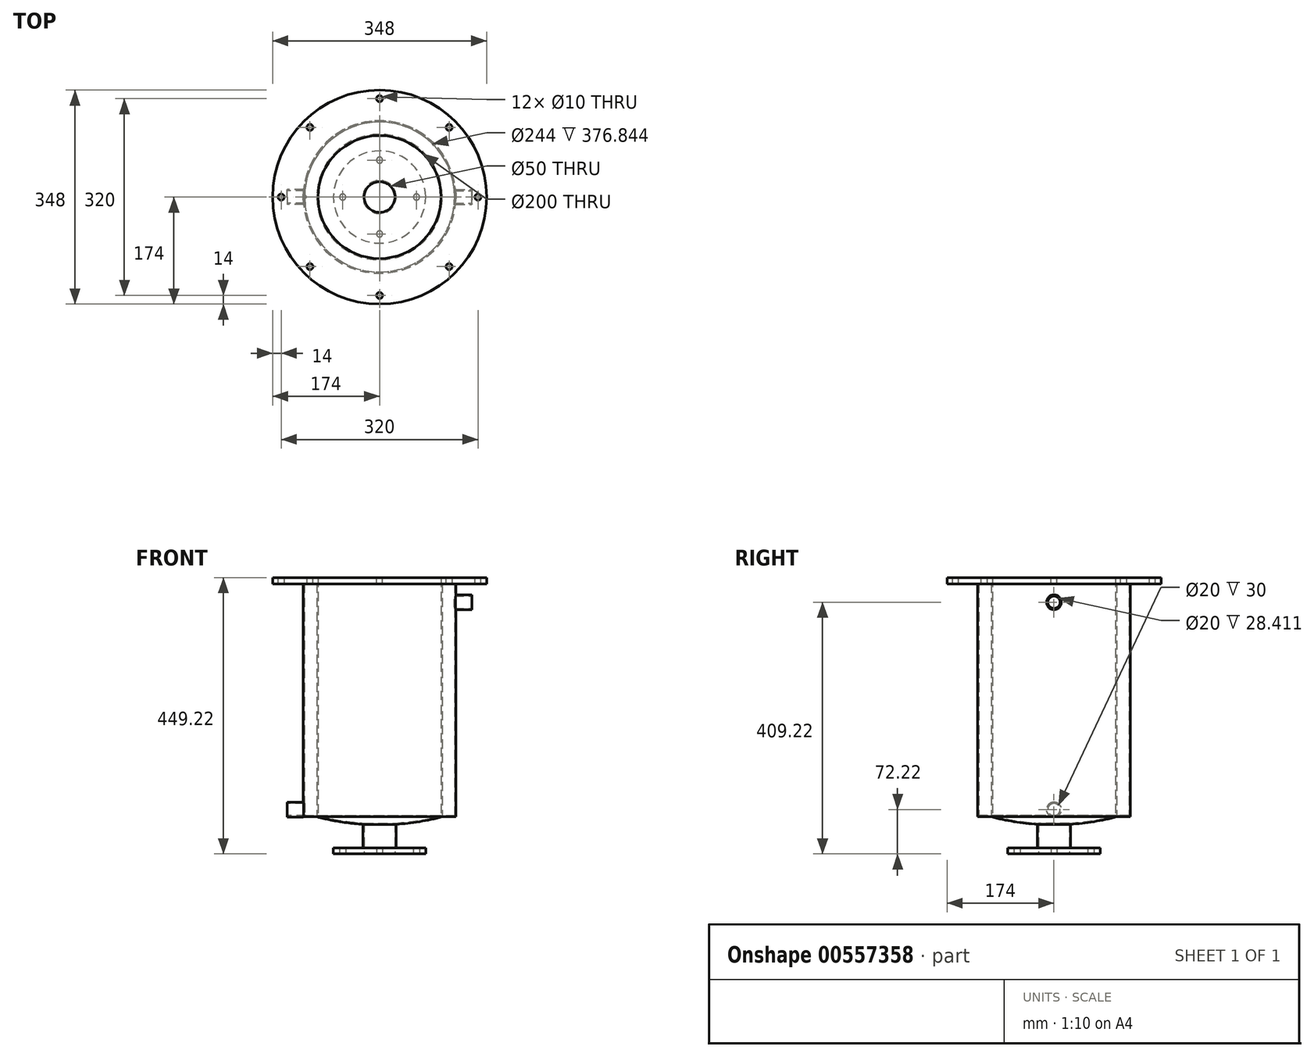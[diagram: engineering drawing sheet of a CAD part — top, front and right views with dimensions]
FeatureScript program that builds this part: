
annotation { "Feature Type Name" : "Feature", "Feature Type Description" : "" }
export const myFeature = defineFeature(function(context is Context, id is Id, definition is map)
    precondition{}
    {
        {
            var Q0;
            Q0=qCreatedBy(makeId("Front.planeOp"),FACE);
            var sketch = newSketch(context, id + "F0", { "sketchPlane" : qUnion([Q0])});
            skLineSegment(sketch, "E0", {"start": v(0, 0) * mm, "end": v(0, 400) * mm, "construction": true});
            skLineSegment(sketch, "E1", {"start": v(-100, 400) * mm, "end": v(-100, 12.7) * mm});
            skArc(sketch, "E2", {"start": v(-25, 0.78) * mm, "mid": v(-62.78, 4.96) * mm, "end": v(-100, 12.7) * mm});
            skLineSegment(sketch, "E3", {"start": v(-25, -49.22) * mm, "end": v(-25, 0.78) * mm});
            skPoint(sketch, "E4.orphan", {"position": v(-25, 22.92) * mm});
            skLineSegment(sketch, "E5.0", {"start": v(-27, -39.22) * mm, "end": v(-27, -1.1) * mm});
            skArc(sketch, "E5.1", {"start": v(-27, -1.1) * mm, "mid": v(-64.8, 3.26) * mm, "end": v(-102, 11.16) * mm});
            skLineSegment(sketch, "E5.2", {"start": v(-102, 390) * mm, "end": v(-102, 13.16) * mm});
            skLineSegment(sketch, "E6", {"start": v(-102, 400) * mm, "end": v(-100, 400) * mm});
            skLineSegment(sketch, "E7", {"start": v(-102, 11.16) * mm, "end": v(-124, 11.16) * mm});
            skLineSegment(sketch, "E8", {"start": v(-124, 11.16) * mm, "end": v(-124, 390) * mm});
            skLineSegment(sketch, "E9", {"start": v(-124, 400) * mm, "end": v(-102, 400) * mm});
            skLineSegment(sketch, "E10.1", {"start": v(-122, 13.16) * mm, "end": v(-122, 390) * mm});
            skLineSegment(sketch, "E10.2", {"start": v(-102, 13.16) * mm, "end": v(-122, 13.16) * mm});
            skLineSegment(sketch, "E11", {"start": v(-124, 400) * mm, "end": v(-174, 400) * mm});
            skLineSegment(sketch, "E12", {"start": v(-174, 400) * mm, "end": v(-174, 390) * mm});
            skLineSegment(sketch, "E13", {"start": v(-174, 390) * mm, "end": v(-124, 390) * mm});
            skLineSegment(sketch, "E14", {"start": v(-122, 390) * mm, "end": v(-102, 390) * mm});
            skLineSegment(sketch, "E15", {"start": v(-25, -49.22) * mm, "end": v(-75, -49.22) * mm});
            skLineSegment(sketch, "E16", {"start": v(-75, -49.22) * mm, "end": v(-75, -39.22) * mm});
            skLineSegment(sketch, "E17", {"start": v(-75, -39.22) * mm, "end": v(-27, -39.22) * mm});
            skSolve(sketch);
        }
        {
            var Q0;
            Q0=makeQuery(id+"F0.imprint","IMPRINT",FACE,{"disambiguationData":[TD([[makeQuery(id+"F0.imprint","IMPRINT",EDGE,{"derivedFrom":sQuery(id+"F0.wireOp",EDGE,"E1")}),-1.0]])]});
            var Q1;
            Q1=sQuery(id+"F0.wireOp",EDGE,"E0");
            revolve(context, id + "F1", {"surfaceOperationType" : NewSurfaceOperationType.NEW, "entities" : qUnion([Q0]), "axis" : qUnion([Q1]), "revolveType" : RevolveType.FULL});
        }
        {
            var Q0;
            Q0=qCreatedBy(makeId("Front.planeOp"),FACE);
            var sketch = newSketch(context, id + "F2", { "sketchPlane" : qUnion([Q0])});
            skLineSegment(sketch, "E18", {"start": v(0, 23) * mm, "end": v(-150, 23) * mm});
            skSolve(sketch);
        }
        {
            var Q0;
            Q0=qCreatedBy(makeId("Right.planeOp"),FACE);
            cPlane(context, id + "F3", {"entities" : qUnion([Q0]), "cplaneType" : CPlaneType.OFFSET, "offset" : 150 * mm, "oppositeDirection" : true, "width" : 150 * mm, "height" : 150 * mm});
        }
        {
            var Q0;
            Q0=qCreatedBy(id+"F3.planeOp",FACE);
            var sketch = newSketch(context, id + "F4", { "sketchPlane" : qUnion([Q0])});
            skCircle(sketch, "E19", {"center": v(0, 23) * mm, "radius": 10 * mm});
            skSolve(sketch);
        }
        {
            var Q0;
            Q0=qCreatedBy(id+"F3.planeOp",FACE);
            var sketch = newSketch(context, id + "F5", { "sketchPlane" : qUnion([Q0])});
            skCircle(sketch, "E20", {"center": v(0, 23) * mm, "radius": 12 * mm});
            skSolve(sketch);
        }
        {
            var Q0;
            Q0=makeQuery(id+"F5.imprint","IMPRINT",FACE,{"disambiguationData":[TD([[makeQuery(id+"F5.imprint","IMPRINT",EDGE,{"derivedFrom":sQuery(id+"F5.wireOp",EDGE,"E20")}),1.0]])]});
            var Q1;
            Q1=makeQuery(id+"F1.opRevolve","SWEPT_FACE",FACE,{"disambiguationData":[OSD([sQuery(id+"F0.wireOp",EDGE,"E8")])]});
            extrude(context, id + "F6", {"entities" : qUnion([Q0]), "operationType" : NewBodyOperationType.ADD, "endBound" : BoundingType.UP_TO_SURFACE, "depth" : 25 * mm, "endBoundEntityFace" : qUnion([Q1]), "offsetDistance" : 25 * mm});
        }
        {
            var Q0;
            Q0=makeQuery(id+"F4.imprint","IMPRINT",FACE,{"disambiguationData":[TD([[makeQuery(id+"F4.imprint","IMPRINT",EDGE,{"derivedFrom":sQuery(id+"F4.wireOp",EDGE,"E19")}),1.0]])]});
            extrude(context, id + "F7", {"entities" : qUnion([Q0]), "operationType" : NewBodyOperationType.REMOVE, "depth" : 30 * mm, "offsetDistance" : 25 * mm});
        }
        {
            var Q0;
            Q0=qCreatedBy(makeId("Right.planeOp"),FACE);
            cPlane(context, id + "F8", {"entities" : qUnion([Q0]), "cplaneType" : CPlaneType.OFFSET, "offset" : 150 * mm, "width" : 150 * mm, "height" : 150 * mm});
        }
        {
            var Q0;
            Q0=qCreatedBy(id+"F8.planeOp",FACE);
            var sketch = newSketch(context, id + "F9", { "sketchPlane" : qUnion([Q0])});
            skCircle(sketch, "E21", {"center": v(0, 360) * mm, "radius": 12 * mm});
            skCircle(sketch, "E22", {"center": v(0, 360) * mm, "radius": 10 * mm});
            skSolve(sketch);
        }
        {
            var Q0;
            Q0=makeQuery(id+"F9.imprint","IMPRINT",FACE,{"disambiguationData":[TD([[makeQuery(id+"F9.imprint","IMPRINT",EDGE,{"derivedFrom":sQuery(id+"F9.wireOp",EDGE,"E21")}),1.0]])]});
            var Q1;
            Q1=makeQuery(id+"F1.opRevolve","SWEPT_FACE",FACE,{"disambiguationData":[OSD([sQuery(id+"F0.wireOp",EDGE,"E8")])]});
            extrude(context, id + "F10", {"entities" : qUnion([Q0]), "operationType" : NewBodyOperationType.ADD, "endBound" : BoundingType.UP_TO_SURFACE, "oppositeDirection" : true, "depth" : 25 * mm, "endBoundEntityFace" : qUnion([Q1]), "offsetDistance" : 25 * mm});
        }
        {
            var Q0;
            Q0=qCreatedBy(id+"F8.planeOp",FACE);
            var sketch = newSketch(context, id + "F11", { "sketchPlane" : qUnion([Q0])});
            skCircle(sketch, "E23", {"center": v(0, 360) * mm, "radius": 10 * mm});
            skSolve(sketch);
        }
        {
            var Q0;
            Q0=makeQuery(id+"F11.imprint","IMPRINT",FACE,{"disambiguationData":[TD([[makeQuery(id+"F11.imprint","IMPRINT",EDGE,{"derivedFrom":sQuery(id+"F11.wireOp",EDGE,"E23")}),1.0]])]});
            extrude(context, id + "F12", {"entities" : qUnion([Q0]), "operationType" : NewBodyOperationType.REMOVE, "oppositeDirection" : true, "depth" : 30 * mm, "offsetDistance" : 25 * mm});
        }
        {
            var Q0;
            Q0=makeQuery(id+"F1.opRevolve","SWEPT_FACE",FACE,{"disambiguationData":[OSD([sQuery(id+"F0.wireOp",EDGE,"E15")])]});
            var sketch = newSketch(context, id + "F13", { "sketchPlane" : qUnion([Q0])});
            skCircle(sketch, "E24", {"center": v(0, 60) * mm, "radius": 5 * mm});
            skCircle(sketch, "E25.1.0", {"center": v(-60, 0) * mm, "radius": 5 * mm});
            skCircle(sketch, "E25.2.0", {"center": v(0, -60) * mm, "radius": 5 * mm});
            skCircle(sketch, "E25.3.0", {"center": v(60, 0) * mm, "radius": 5 * mm});
            skPoint(sketch, "E25.center", {"position": v(0, 0) * mm});
            skSolve(sketch);
        }
        {
            var Q0;
            Q0=makeQuery(id+"F13.imprint","IMPRINT",FACE,{"disambiguationData":[TD([[makeQuery(id+"F13.imprint","IMPRINT",EDGE,{"derivedFrom":sQuery(id+"F13.wireOp",EDGE,"E24")}),1.0]])]});
            var Q1;
            Q1=makeQuery(id+"F13.imprint","IMPRINT",FACE,{"disambiguationData":[TD([[makeQuery(id+"F13.imprint","IMPRINT",EDGE,{"derivedFrom":sQuery(id+"F13.wireOp",EDGE,"E25.3.0")}),1.0]])]});
            var Q2;
            Q2=makeQuery(id+"F13.imprint","IMPRINT",FACE,{"disambiguationData":[TD([[makeQuery(id+"F13.imprint","IMPRINT",EDGE,{"derivedFrom":sQuery(id+"F13.wireOp",EDGE,"E25.2.0")}),1.0]])]});
            var Q3;
            Q3=makeQuery(id+"F13.imprint","IMPRINT",FACE,{"disambiguationData":[TD([[makeQuery(id+"F13.imprint","IMPRINT",EDGE,{"derivedFrom":sQuery(id+"F13.wireOp",EDGE,"E25.1.0")}),1.0]])]});
            var Q4;
            Q4=makeQuery(id+"F1.opRevolve","SWEPT_FACE",FACE,{"disambiguationData":[OSD([sQuery(id+"F0.wireOp",EDGE,"E17")])]});
            extrude(context, id + "F14", {"entities" : qUnion([Q0, Q1, Q2, Q3]), "operationType" : NewBodyOperationType.REMOVE, "endBound" : BoundingType.UP_TO_SURFACE, "oppositeDirection" : true, "depth" : 25 * mm, "endBoundEntityFace" : qUnion([Q4]), "offsetDistance" : 25 * mm});
        }
        {
            var Q0;
            Q0=makeQuery(id+"F1.opRevolve","SWEPT_FACE",FACE,{"disambiguationData":[OSD([sQuery(id+"F0.wireOp",EDGE,"E6"),sQuery(id+"F0.wireOp",EDGE,"E9"),sQuery(id+"F0.wireOp",EDGE,"E11")])]});
            var sketch = newSketch(context, id + "F15", { "sketchPlane" : qUnion([Q0])});
            skCircle(sketch, "E26", {"center": v(0, 160) * mm, "radius": 5 * mm});
            skCircle(sketch, "E27.1.0", {"center": v(-113.14, 113.14) * mm, "radius": 5 * mm});
            skCircle(sketch, "E27.2.0", {"center": v(-160, 0) * mm, "radius": 5 * mm});
            skCircle(sketch, "E27.3.0", {"center": v(-113.14, -113.14) * mm, "radius": 5 * mm});
            skCircle(sketch, "E27.4.0", {"center": v(0, -160) * mm, "radius": 5 * mm});
            skCircle(sketch, "E27.5.0", {"center": v(113.14, -113.14) * mm, "radius": 5 * mm});
            skCircle(sketch, "E27.6.0", {"center": v(160, 0) * mm, "radius": 5 * mm});
            skCircle(sketch, "E27.7.0", {"center": v(113.14, 113.14) * mm, "radius": 5 * mm});
            skPoint(sketch, "E27.center", {"position": v(0, 0) * mm});
            skSolve(sketch);
        }
        {
            var Q0;
            Q0 = qSketchRegion(id + "F15", true);
            var Q1;
            Q1=makeQuery(id+"F1.opRevolve","SWEPT_FACE",FACE,{"disambiguationData":[OSD([sQuery(id+"F0.wireOp",EDGE,"E13")])]});
            extrude(context, id + "F16", {"entities" : qUnion([Q0]), "operationType" : NewBodyOperationType.REMOVE, "endBound" : BoundingType.UP_TO_SURFACE, "oppositeDirection" : true, "depth" : 25 * mm, "endBoundEntityFace" : qUnion([Q1]), "offsetDistance" : 25 * mm});
        }
    });
